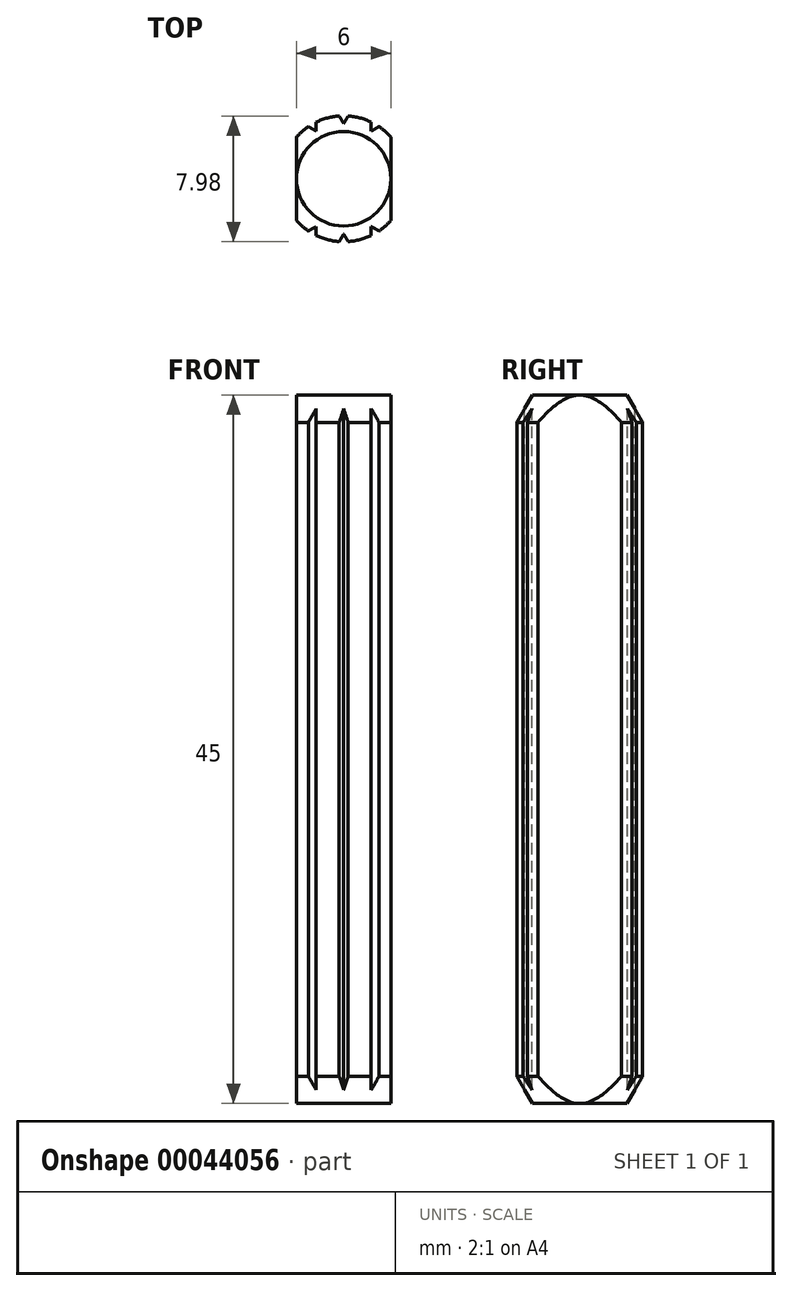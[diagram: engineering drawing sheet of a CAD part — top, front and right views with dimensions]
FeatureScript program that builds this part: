
annotation { "Feature Type Name" : "Feature", "Feature Type Description" : "" }
export const myFeature = defineFeature(function(context is Context, id is Id, definition is map)
    precondition{}
    {
        {
            var Q0;
            Q0=qCreatedBy(makeId("Front.planeOp"),FACE);
            var sketch = newSketch(context, id + "F0", { "sketchPlane" : qUnion([Q0])});
            skLineSegment(sketch, "E0", {"start": v(0, 0) * mm, "end": v(-3, 0) * mm});
            skLineSegment(sketch, "E1", {"start": v(-3, 0) * mm, "end": v(-4, 1.73) * mm});
            skLineSegment(sketch, "E2", {"start": v(-4, 1.73) * mm, "end": v(-4, 43.27) * mm});
            skLineSegment(sketch, "E3", {"start": v(-4, 43.27) * mm, "end": v(-3, 45) * mm});
            skLineSegment(sketch, "E4", {"start": v(-3, 45) * mm, "end": v(0, 45) * mm});
            skLineSegment(sketch, "E5", {"start": v(0, 45) * mm, "end": v(0, 0) * mm});
            skSolve(sketch);
        }
        {
            var Q0;
            Q0=makeQuery(id+"F0.imprint","IMPRINT",FACE,{"disambiguationData":[TD([[makeQuery(id+"F0.imprint","IMPRINT",EDGE,{"derivedFrom":sQuery(id+"F0.wireOp",EDGE,"E0")}),-1.0]])]});
            var Q1;
            Q1=sQuery(id+"F0.wireOp",EDGE,"E5");
            revolve(context, id + "F1", {"entities" : qUnion([Q0]), "axis" : qUnion([Q1]), "revolveType" : RevolveType.FULL});
        }
        {
            var Q0;
            Q0=makeQuery(id+"F1.opRevolve","SWEPT_FACE",FACE,{"disambiguationData":[OSD([sQuery(id+"F0.wireOp",EDGE,"E4")])]});
            var sketch = newSketch(context, id + "F2", { "sketchPlane" : qUnion([Q0])});
            skLineSegment(sketch, "E6.bottom", {"start": v(-3, 5) * mm, "end": v(3, 5) * mm});
            skLineSegment(sketch, "E6.top", {"start": v(-3, -5) * mm, "end": v(3, -5) * mm});
            skLineSegment(sketch, "E6.left", {"start": v(-3, 5) * mm, "end": v(-3, -5) * mm});
            skLineSegment(sketch, "E6.right", {"start": v(3, 5) * mm, "end": v(3, -5) * mm});
            skCircle(sketch, "E7", {"center": v(0, 0) * mm, "radius": 5.83 * mm});
            skSolve(sketch);
        }
        {
            var Q0;
            {var subQ0=sQuery(id+"F2.wireOp",EDGE,"E7");var subQ1=sQuery(id+"F2.wireOp",EDGE,"E6.left");var subQ3=makeQuery(id+"F2.imprint","INTERSECT",VERTEX,{"derivedFrom":[sQuery(id+"F2.wireOp",EDGE,"E6.bottom"),subQ1,subQ0]});Q0=makeQuery(id+"F2.imprint","IMPRINT",FACE,{"disambiguationData":[TD([[makeQuery(id+"F2.imprint","IMPRINT",EDGE,{"disambiguationData":[TD([[subQ3,-1.0]])],"derivedFrom":subQ1}),-1.0]])]});}
            var Q1;
            {var subQ0=sQuery(id+"F2.wireOp",EDGE,"E7");var subQ1=sQuery(id+"F2.wireOp",EDGE,"E6.right");var subQ3=makeQuery(id+"F2.imprint","INTERSECT",VERTEX,{"derivedFrom":[sQuery(id+"F2.wireOp",EDGE,"E6.bottom"),subQ1,subQ0]});Q1=makeQuery(id+"F2.imprint","IMPRINT",FACE,{"disambiguationData":[TD([[makeQuery(id+"F2.imprint","IMPRINT",EDGE,{"disambiguationData":[TD([[subQ3,-1.0]])],"derivedFrom":subQ1}),1.0]])]});}
            extrude(context, id + "F3", {"entities" : qUnion([Q0, Q1]), "operationType" : NewBodyOperationType.REMOVE, "endBound" : BoundingType.THROUGH_ALL, "oppositeDirection" : true, "depth" : 25 * mm});
        }
        {
            var Q0;
            Q0=makeQuery(id+"F1.opRevolve","SWEPT_FACE",FACE,{"disambiguationData":[OSD([sQuery(id+"F0.wireOp",EDGE,"E4")])]});
            var sketch = newSketch(context, id + "F4", { "sketchPlane" : qUnion([Q0])});
            skLineSegment(sketch, "E8", {"start": v(-0.81, 4.9) * mm, "end": v(0, 3.5) * mm});
            skPoint(sketch, "E8.endSnap0", {"position": v(0, 3) * mm});
            skLineSegment(sketch, "E9", {"start": v(0, 3.5) * mm, "end": v(0.81, 4.9) * mm});
            skLineSegment(sketch, "E10", {"start": v(-0.81, 4.9) * mm, "end": v(0.81, 4.9) * mm});
            skLineSegment(sketch, "E11.MirrorCS", {"start": v(0, -3.5) * mm, "end": v(0.81, -4.9) * mm});
            skLineSegment(sketch, "E12.MirrorCS", {"start": v(-0.81, -4.9) * mm, "end": v(0, -3.5) * mm});
            skLineSegment(sketch, "E13.MirrorCS", {"start": v(-0.81, -4.9) * mm, "end": v(0.81, -4.9) * mm});
            skSolve(sketch);
        }
        {
            var Q0;
            Q0=makeQuery(id+"F4.imprint","IMPRINT",FACE,{"disambiguationData":[TD([[makeQuery(id+"F4.imprint","IMPRINT",EDGE,{"derivedFrom":sQuery(id+"F4.wireOp",EDGE,"E8")}),1.0]])]});
            var Q1;
            Q1=makeQuery(id+"F4.imprint","IMPRINT",FACE,{"disambiguationData":[TD([[makeQuery(id+"F4.imprint","IMPRINT",EDGE,{"derivedFrom":sQuery(id+"F4.wireOp",EDGE,"E11.MirrorCS")}),-1.0]])]});
            extrude(context, id + "F5", {"entities" : qUnion([Q0, Q1]), "operationType" : NewBodyOperationType.REMOVE, "endBound" : BoundingType.THROUGH_ALL, "oppositeDirection" : true, "depth" : 25 * mm});
        }
        {
            var Q0;
            Q0=makeQuery(id+"F5.boolean.opBoolean","COPY",FACE,{"derivedFrom":makeQuery(id+"F5.opExtrude","SWEPT_FACE",FACE,{"disambiguationData":[OSD([sQuery(id+"F4.wireOp",EDGE,"E9")])]})});
            var Q1;
            Q1=makeQuery(id+"F5.boolean.opBoolean","COPY",FACE,{"derivedFrom":makeQuery(id+"F5.opExtrude","SWEPT_FACE",FACE,{"disambiguationData":[OSD([sQuery(id+"F4.wireOp",EDGE,"E8")])]})});
            var Q2;
            Q2=makeQuery(id+"F3.boolean.opBoolean","SPLIT",EDGE,{"disambiguationData":[OD(0.0)],"derivedFrom":makeQuery(id+"F1.opRevolve","SWEPT_EDGE",EDGE,{"disambiguationData":[OSD([sQuery(id+"F0.wireOp",EDGE,"E3"),sQuery(id+"F0.wireOp",EDGE,"E4")])]})});
            circularPattern(context, id + "F6", {"faces" : qUnion([Q0, Q1]), "axis" : qUnion([Q2]), "angle" : 360 * degree, "instanceCount" : 12, "equalSpace" : true, "patternType" : PatternType.FACE});
        }
        {
            var Q0;
            Q0=makeQuery(id+"F5.boolean.opBoolean","COPY",FACE,{"derivedFrom":makeQuery(id+"F5.opExtrude","SWEPT_FACE",FACE,{"disambiguationData":[OSD([sQuery(id+"F4.wireOp",EDGE,"E11.MirrorCS")])]})});
            var Q1;
            Q1=makeQuery(id+"F5.boolean.opBoolean","COPY",FACE,{"derivedFrom":makeQuery(id+"F5.opExtrude","SWEPT_FACE",FACE,{"disambiguationData":[OSD([sQuery(id+"F4.wireOp",EDGE,"E12.MirrorCS")])]})});
            var Q2;
            Q2=makeQuery(id+"F3.boolean.opBoolean","SPLIT",EDGE,{"disambiguationData":[OD(1.0)],"derivedFrom":makeQuery(id+"F1.opRevolve","SWEPT_EDGE",EDGE,{"disambiguationData":[OSD([sQuery(id+"F0.wireOp",EDGE,"E3"),sQuery(id+"F0.wireOp",EDGE,"E4")])]})});
            circularPattern(context, id + "F7", {"faces" : qUnion([Q0, Q1]), "axis" : qUnion([Q2]), "angle" : 360 * degree, "instanceCount" : 12, "oppositeDirection" : true, "equalSpace" : true, "patternType" : PatternType.FACE});
        }
    });
